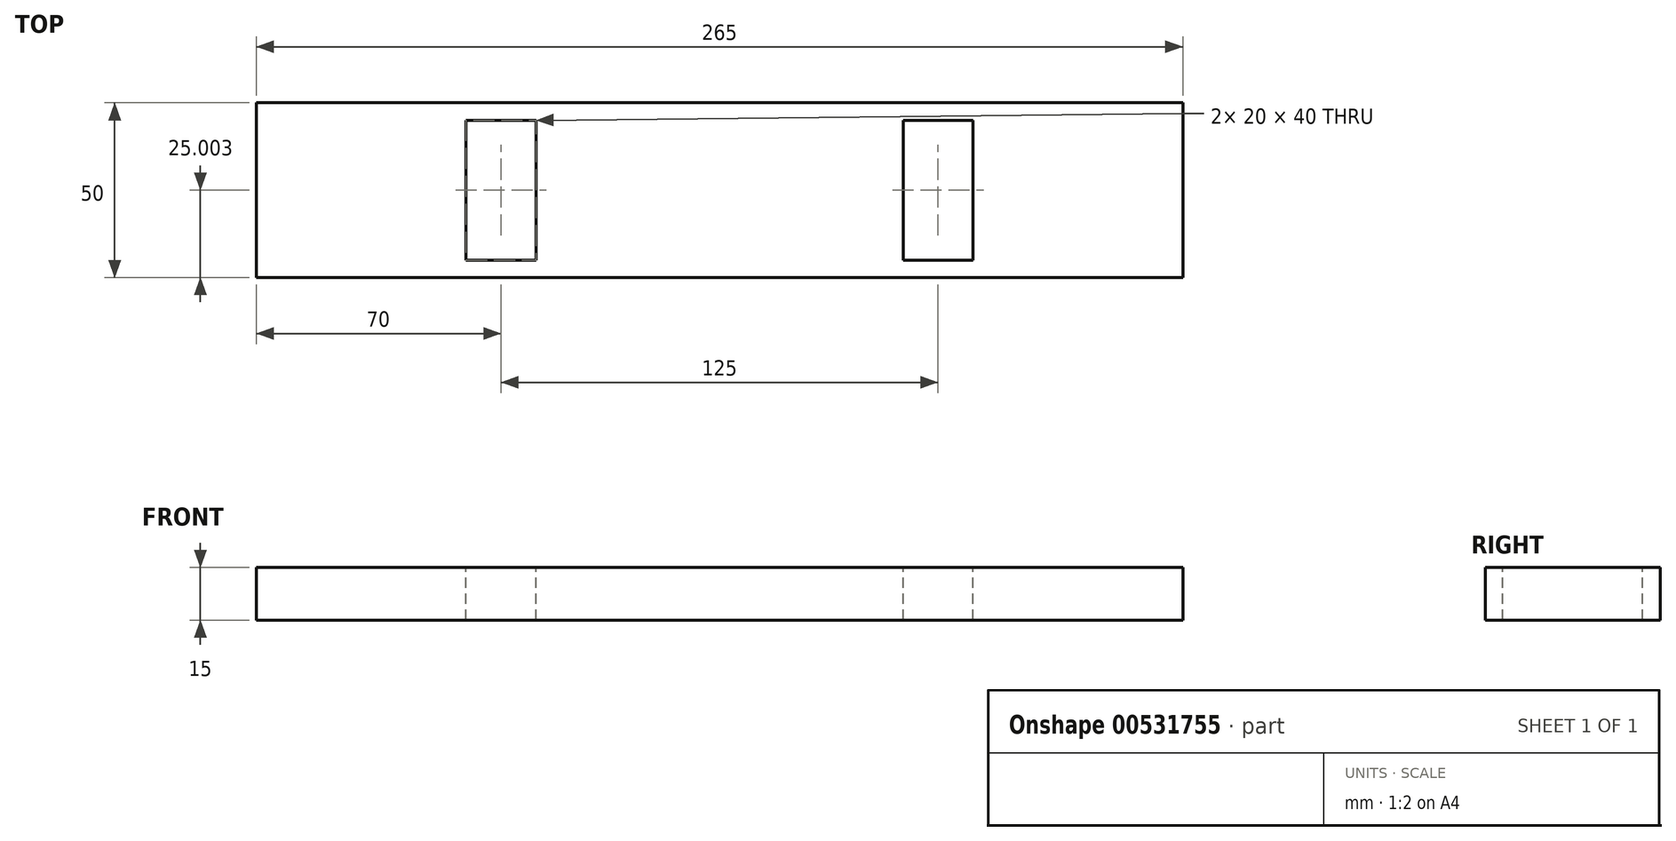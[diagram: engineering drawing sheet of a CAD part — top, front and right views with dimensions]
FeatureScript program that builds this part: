
annotation { "Feature Type Name" : "Feature", "Feature Type Description" : "" }
export const myFeature = defineFeature(function(context is Context, id is Id, definition is map)
    precondition{}
    {
        {
            var Q0;
            Q0=qCreatedBy(makeId("Top.planeOp"),FACE);
            var sketch = newSketch(context, id + "F0", { "sketchPlane" : qUnion([Q0])});
            skLineSegment(sketch, "E0.bottom", {"start": v(132.5, -23.37) * mm, "end": v(-132.5, -23.37) * mm});
            skLineSegment(sketch, "E0.top", {"start": v(132.5, 26.63) * mm, "end": v(-132.5, 26.63) * mm});
            skLineSegment(sketch, "E0.left", {"start": v(132.5, -23.37) * mm, "end": v(132.5, 26.63) * mm});
            skLineSegment(sketch, "E0.right", {"start": v(-132.5, -23.37) * mm, "end": v(-132.5, 26.63) * mm});
            skPoint(sketch, "E0.middle", {"position": v(0, 1.63) * mm});
            skSolve(sketch);
        }
        {
            var Q0;
            Q0 = qSketchRegion(id + "F0", true);
            extrude(context, id + "F1", {"entities" : qUnion([Q0]), "depth" : 15 * mm, "offsetDistance" : 25 * mm});
        }
        {
            var Q0;
            Q0=makeQuery(id+"F1.opExtrude","CAP_FACE",FACE,{"disambiguationData":[OSD([sQuery(id+"F0.wireOp",EDGE,"E0.bottom"),sQuery(id+"F0.wireOp",EDGE,"E0.top"),sQuery(id+"F0.wireOp",EDGE,"E0.left"),sQuery(id+"F0.wireOp",EDGE,"E0.right")])],"isStart":false});
            var sketch = newSketch(context, id + "F2", { "sketchPlane" : qUnion([Q0])});
            skLineSegment(sketch, "E1", {"start": v(-132.5, -23.37) * mm, "end": v(-72.5, -23.37) * mm});
            skLineSegment(sketch, "E2", {"start": v(-72.5, -23.37) * mm, "end": v(-72.5, -18.37) * mm});
            skLineSegment(sketch, "E3", {"start": v(-72.5, -18.37) * mm, "end": v(-72.5, 21.63) * mm});
            skLineSegment(sketch, "E4", {"start": v(-72.5, 21.63) * mm, "end": v(-52.5, 21.63) * mm});
            skLineSegment(sketch, "E5", {"start": v(-52.5, 21.63) * mm, "end": v(-52.5, -18.37) * mm});
            skLineSegment(sketch, "E6", {"start": v(-52.5, -18.37) * mm, "end": v(-72.5, -18.37) * mm});
            skLineSegment(sketch, "E7", {"start": v(132.5, -23.37) * mm, "end": v(72.5, -23.37) * mm});
            skLineSegment(sketch, "E8", {"start": v(72.5, -23.37) * mm, "end": v(72.5, -18.37) * mm});
            skLineSegment(sketch, "E9.bottom", {"start": v(72.5, -18.37) * mm, "end": v(52.5, -18.37) * mm});
            skLineSegment(sketch, "E9.top", {"start": v(72.5, 21.63) * mm, "end": v(52.5, 21.63) * mm});
            skLineSegment(sketch, "E9.left", {"start": v(72.5, -18.37) * mm, "end": v(72.5, 21.63) * mm});
            skLineSegment(sketch, "E9.right", {"start": v(52.5, -18.37) * mm, "end": v(52.5, 21.63) * mm});
            skSolve(sketch);
        }
        {
            var Q0;
            Q0 = qSketchRegion(id + "F2", true);
            extrude(context, id + "F3", {"entities" : qUnion([Q0]), "operationType" : NewBodyOperationType.REMOVE, "oppositeDirection" : true, "depth" : 39.9 * mm, "offsetDistance" : 25 * mm});
        }
        {
            var Q0;
            Q0 = qSketchRegion(id + "F2", true);
            extrude(context, id + "F4", {"entities" : qUnion([Q0]), "operationType" : NewBodyOperationType.REMOVE, "oppositeDirection" : true, "depth" : 35.1 * mm, "offsetDistance" : 25 * mm});
        }
    });
